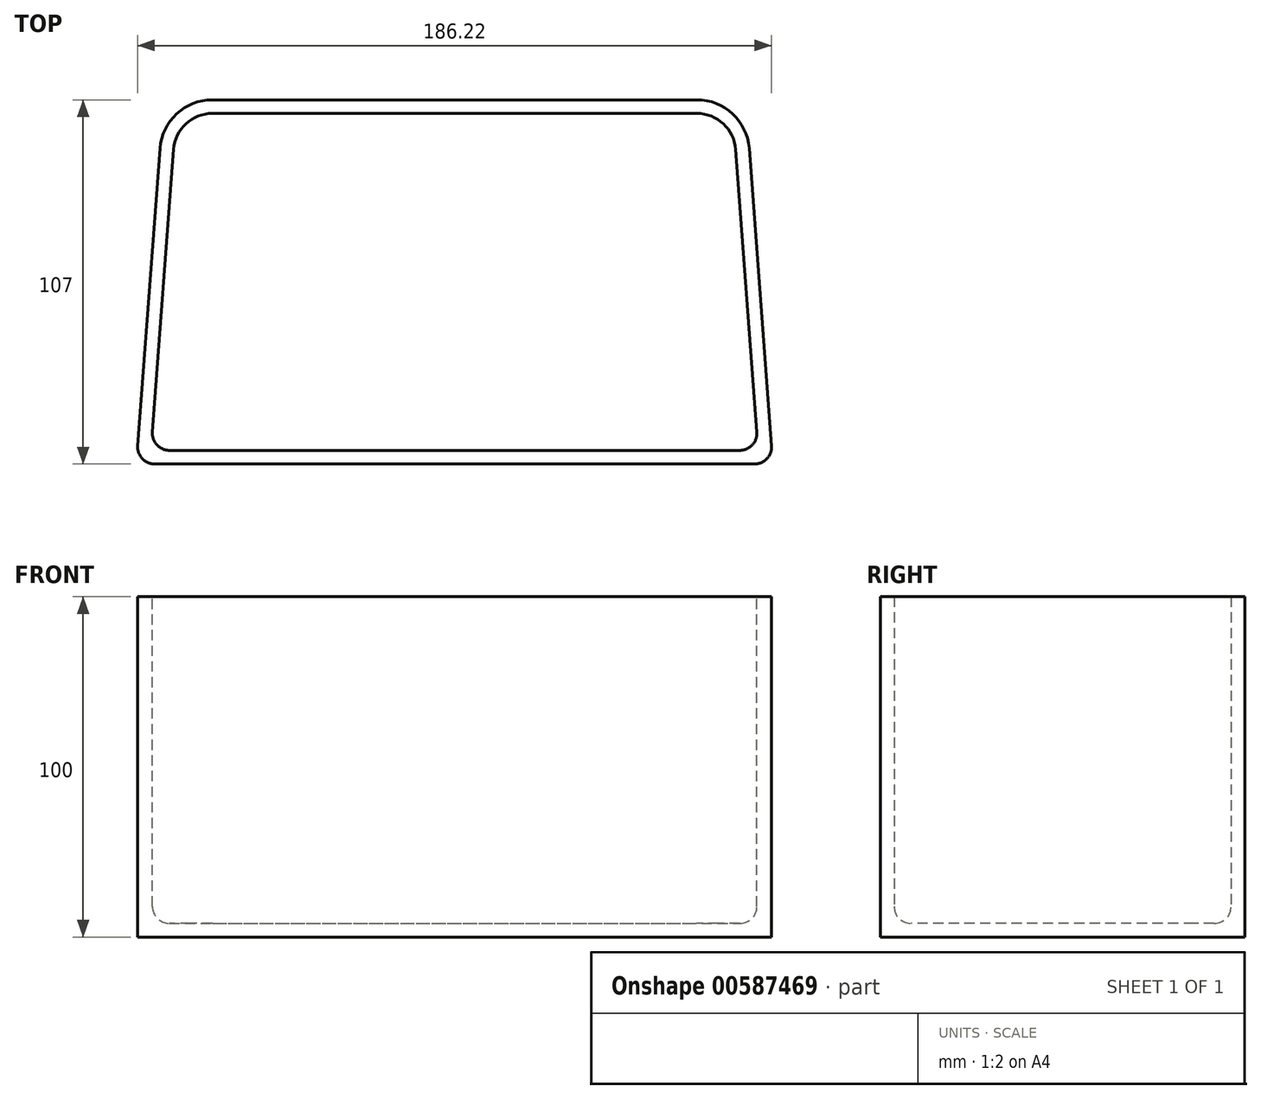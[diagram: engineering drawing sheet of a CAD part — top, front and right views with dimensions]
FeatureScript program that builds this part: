
annotation { "Feature Type Name" : "Feature", "Feature Type Description" : "" }
export const myFeature = defineFeature(function(context is Context, id is Id, definition is map)
    precondition{}
    {
        {
            var Q0;
            Q0=qCreatedBy(makeId("Top.planeOp"),FACE);
            var sketch = newSketch(context, id + "F0", { "sketchPlane" : qUnion([Q0])});
            skLineSegment(sketch, "E0", {"start": v(-81.88, -40.8) * mm, "end": v(105.12, -40.8) * mm});
            skLineSegment(sketch, "E1", {"start": v(105.12, -40.8) * mm, "end": v(98.15, 51.94) * mm});
            skLineSegment(sketch, "E2", {"start": v(-74.9, 51.94) * mm, "end": v(-81.88, -40.8) * mm});
            skLineSegment(sketch, "E3", {"start": v(-59.53, 66.2) * mm, "end": v(82.78, 66.2) * mm});
            skPoint(sketch, "E4.visualSharp", {"position": v(-73.83, 66.2) * mm});
            skArc(sketch, "E4.filletArc", {"start": v(-59.53, 66.2) * mm, "mid": v(-70.01, 62.09) * mm, "end": v(-74.9, 51.94) * mm});
            skPoint(sketch, "E5.visualSharp", {"position": v(97.08, 66.2) * mm});
            skArc(sketch, "E5.filletArc", {"start": v(98.15, 51.94) * mm, "mid": v(93.26, 62.09) * mm, "end": v(82.78, 66.2) * mm});
            skSolve(sketch);
        }
        {
            var Q0;
            Q0=makeQuery(id+"F0.imprint","IMPRINT",FACE,{"disambiguationData":[TD([[makeQuery(id+"F0.imprint","IMPRINT",EDGE,{"derivedFrom":sQuery(id+"F0.wireOp",EDGE,"E0")}),1.0]])]});
            extrude(context, id + "F1", {"entities" : qUnion([Q0]), "depth" : 100 * mm, "offsetDistance" : 25 * mm});
        }
        {
            var Q0;
            Q0=makeQuery(id+"F1.opExtrude","CAP_FACE",FACE,{"disambiguationData":[OSD([sQuery(id+"F0.wireOp",EDGE,"E0"),sQuery(id+"F0.wireOp",EDGE,"E1"),sQuery(id+"F0.wireOp",EDGE,"E2"),sQuery(id+"F0.wireOp",EDGE,"E3"),sQuery(id+"F0.wireOp",EDGE,"E4.filletArc"),sQuery(id+"F0.wireOp",EDGE,"E5.filletArc")])],"isStart":false});
            shell(context, id + "F2", {"entities" : qUnion([Q0]), "thickness" : 4 * mm});
        }
        {
            var Q0;
            Q0=makeQuery(id+"F1.opExtrude","SWEPT_EDGE",EDGE,{"disambiguationData":[OSD([sQuery(id+"F0.wireOp",EDGE,"E0"),sQuery(id+"F0.wireOp",EDGE,"E1")])]});
            var Q1;
            Q1=makeQuery(id+"F1.opExtrude","SWEPT_EDGE",EDGE,{"disambiguationData":[OSD([sQuery(id+"F0.wireOp",EDGE,"E0"),sQuery(id+"F0.wireOp",EDGE,"E2")])]});
            var Q2;
            Q2=makeQuery(id+"F2.opShell","OFFSET_EDGE",EDGE,{"disambiguationData":[OSD([sQuery(id+"F0.wireOp",EDGE,"E0"),sQuery(id+"F0.wireOp",EDGE,"E1")])]});
            var Q3;
            Q3=makeQuery(id+"F2.opShell","OFFSET_EDGE",EDGE,{"disambiguationData":[OSD([sQuery(id+"F0.wireOp",EDGE,"E0"),sQuery(id+"F0.wireOp",EDGE,"E2")])]});
            var Q4;
            {var subQ0=sQuery(id+"F0.wireOp",EDGE,"E0");Q4=makeQuery(id+"F2.opShell","OFFSET_EDGE",EDGE,{"disambiguationData":[OSD([subQ0]),TDD([makeQuery(id+"F1.opExtrude","CAP_EDGE",EDGE,{"disambiguationData":[OSD([subQ0])],"isStart":true})])]});}
            var Q5;
            {var subQ0=sQuery(id+"F0.wireOp",EDGE,"E1");Q5=makeQuery(id+"F2.opShell","OFFSET_EDGE",EDGE,{"disambiguationData":[OSD([subQ0]),TDD([makeQuery(id+"F1.opExtrude","CAP_EDGE",EDGE,{"disambiguationData":[OSD([subQ0])],"isStart":true})])]});}
            fillet(context, id + "F3", {"entities" : qUnion([Q0, Q1, Q2, Q3, Q4, Q5]), "radius" : 5 * mm, "tangentPropagation" : true, "allowEdgeOverflow" : false});
        }
    });
